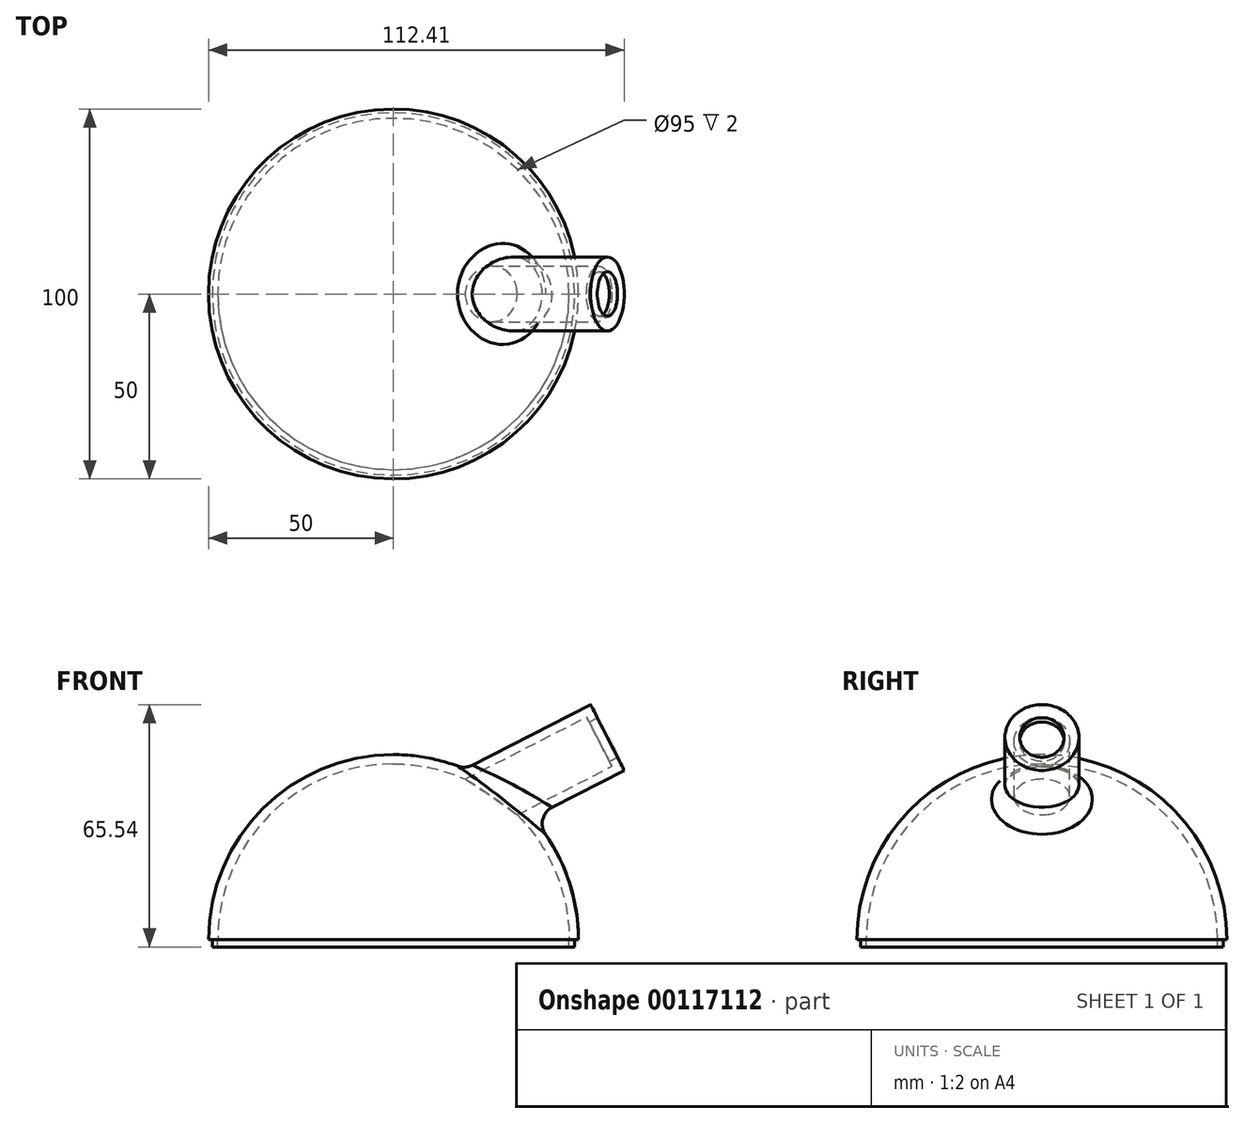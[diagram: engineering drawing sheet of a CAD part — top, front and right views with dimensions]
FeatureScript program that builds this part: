
annotation { "Feature Type Name" : "Feature", "Feature Type Description" : "" }
export const myFeature = defineFeature(function(context is Context, id is Id, definition is map)
    precondition{}
    {
        {
            var Q0;
            Q0=qCreatedBy(makeId("Front.planeOp"),FACE);
            var sketch = newSketch(context, id + "F0", { "sketchPlane" : qUnion([Q0])});
            skLineSegment(sketch, "E0", {"start": v(0, 0) * mm, "end": v(0, 50) * mm});
            skLineSegment(sketch, "E1", {"start": v(0, 0) * mm, "end": v(50, 0) * mm});
            skArc(sketch, "E2", {"start": v(0, 50) * mm, "mid": v(35.36, 35.36) * mm, "end": v(50, 0) * mm});
            skSolve(sketch);
        }
        {
            var Q0;
            Q0=makeQuery(id+"F0.imprint","IMPRINT",FACE,{"disambiguationData":[TD([[makeQuery(id+"F0.imprint","IMPRINT",EDGE,{"derivedFrom":sQuery(id+"F0.wireOp",EDGE,"E0")}),-1.0]])]});
            var Q1;
            Q1=sQuery(id+"F0.wireOp",EDGE,"E0");
            revolve(context, id + "F1", {"entities" : qUnion([Q0]), "axis" : qUnion([Q1]), "revolveType" : RevolveType.FULL});
        }
        {
            var Q0;
            Q0=qCreatedBy(makeId("Front.planeOp"),FACE);
            var sketch = newSketch(context, id + "F2", { "sketchPlane" : qUnion([Q0])});
            skLineSegment(sketch, "E3", {"start": v(0, 0) * mm, "end": v(0, 18.89) * mm});
            skLineSegment(sketch, "E4", {"start": v(5.44, 27.79) * mm, "end": v(57.85, 54.64) * mm});
            skPoint(sketch, "E5.visualSharp", {"position": v(0, 25) * mm});
            skArc(sketch, "E5.filletArc", {"start": v(5.44, 27.79) * mm, "mid": v(1.47, 24.1) * mm, "end": v(0, 18.89) * mm});
            skSolve(sketch);
        }
        {
            var Q0;
            Q0=makeQuery(id+"F1.opRevolve","SWEPT_FACE",FACE,{"disambiguationData":[OSD([sQuery(id+"F0.wireOp",EDGE,"E1")])]});
            var sketch = newSketch(context, id + "F3", { "sketchPlane" : qUnion([Q0])});
            skCircle(sketch, "E6", {"center": v(0, 0) * mm, "radius": 10 * mm});
            skSolve(sketch);
        }
        {
            var Q0;
            Q0=makeQuery(id+"F3.imprint","IMPRINT",FACE,{"disambiguationData":[TD([[makeQuery(id+"F3.imprint","IMPRINT",EDGE,{"derivedFrom":sQuery(id+"F3.wireOp",EDGE,"E6")}),1.0]])]});
            var Q1;
            Q1=sQuery(id+"F2.wireOp",EDGE,"E3");
            var Q2;
            Q2=sQuery(id+"F2.wireOp",EDGE,"E5.filletArc");
            var Q3;
            Q3=sQuery(id+"F2.wireOp",EDGE,"E4");
            sweep(context, id + "F4", {"operationType" : NewBodyOperationType.ADD, "profiles" : qUnion([Q0]), "path" : qUnion([Q1, Q2, Q3])});
        }
        {
            var Q0;
            Q0=makeQuery(id+"F1.opRevolve","SWEPT_FACE",FACE,{"disambiguationData":[OSD([sQuery(id+"F0.wireOp",EDGE,"E1")])]});
            shell(context, id + "F5", {"entities" : qUnion([Q0]), "thickness" : 2.5 * mm});
        }
        {
            var Q0;
            Q0=makeQuery(id+"F1.opRevolve","SWEPT_FACE",FACE,{"disambiguationData":[OSD([sQuery(id+"F0.wireOp",EDGE,"E1")])]});
            var sketch = newSketch(context, id + "F6", { "sketchPlane" : qUnion([Q0])});
            skCircle(sketch, "E7", {"center": v(0, 0) * mm, "radius": 49 * mm});
            skSolve(sketch);
        }
        {
            var Q0;
            Q0=makeQuery(id+"F6.imprint","IMPRINT",FACE,{"disambiguationData":[TD([[makeQuery(id+"F6.imprint","IMPRINT",EDGE,{"derivedFrom":sQuery(id+"F6.wireOp",EDGE,"E7")}),1.0]])]});
            extrude(context, id + "F7", {"entities" : qUnion([Q0]), "operationType" : NewBodyOperationType.ADD, "depth" : 2 * mm});
        }
        {
            var Q0;
            Q0=makeQuery(id+"F4.opSweep","CAP_FACE",FACE,{"disambiguationData":[OSD([sQuery(id+"F2.wireOp",VERTEX,"E4.end"),sQuery(id+"F3.wireOp",EDGE,"E6")])],"isStart":false});
            var sketch = newSketch(context, id + "F8", { "sketchPlane" : qUnion([Q0])});
            skCircle(sketch, "E8", {"center": v(0, 22.25) * mm, "radius": 6 * mm});
            skSolve(sketch);
        }
        {
            var Q0;
            Q0=qSketchRegion(id+"F8",true);
            extrude(context, id + "F9", {"entities" : qUnion([Q0]), "operationType" : NewBodyOperationType.REMOVE, "oppositeDirection" : true, "depth" : 3 * mm});
        }
        {
            var Q0;
            Q0=makeQuery(id+"F4.boolean.opBoolean","INTERSECT",EDGE,{"derivedFrom":[makeQuery(id+"F1.opRevolve","SWEPT_FACE",FACE,{"disambiguationData":[OSD([sQuery(id+"F0.wireOp",EDGE,"E2")])]}),makeQuery(id+"F4.opSweep","SWEPT_FACE",FACE,{"disambiguationData":[OSD([sQuery(id+"F2.wireOp",EDGE,"E4"),sQuery(id+"F3.wireOp",EDGE,"E6")])]})]});
            fillet(context, id + "F10", {"entities" : qUnion([Q0]), "radius" : 5 * mm, "tangentPropagation" : true, "allowEdgeOverflow" : false});
        }
    });
